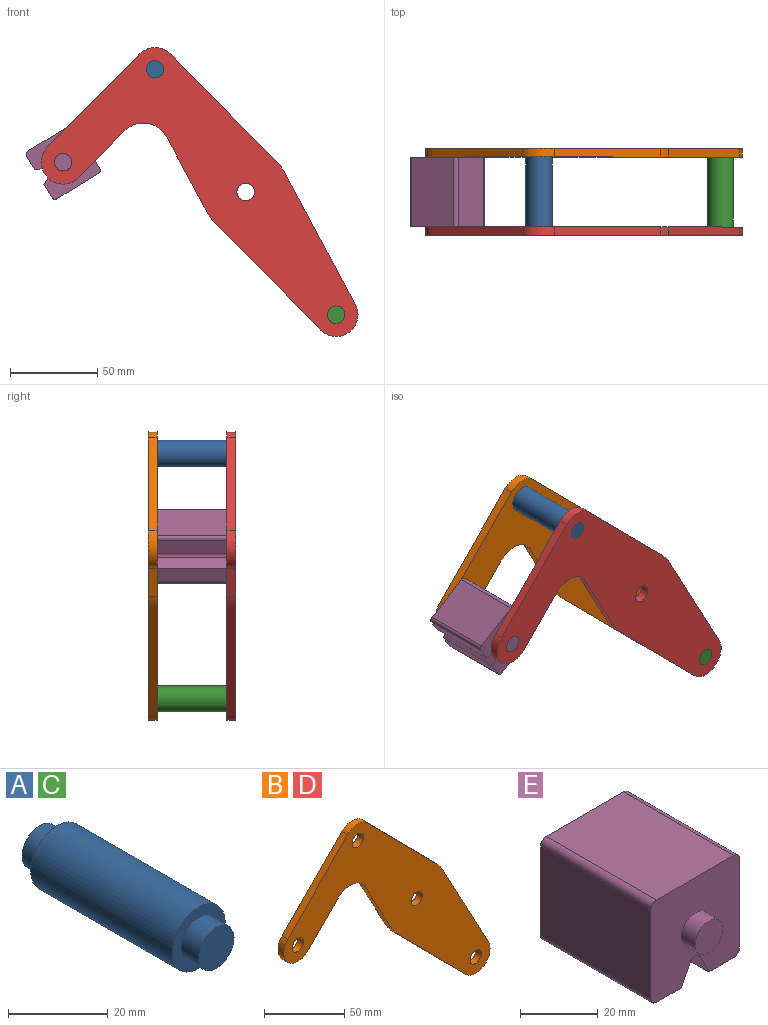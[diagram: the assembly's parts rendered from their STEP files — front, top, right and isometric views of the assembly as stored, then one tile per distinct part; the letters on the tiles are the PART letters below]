
ASSEMBLY  parts=5 mates=3
PART A: 7 faces, bbox 15x50x15 mm
  f0: cylinder r=7.5mm len=40mm, axis (0,-1,0), area 1885mm2, adj f2,f5
  f1: cylinder r=5mm len=10mm, axis (0,1,0), area 157.1mm2, adj f2,f3
  f2: plane 15x15mm, normal (0,-1,0), area 98.2mm2, adj f0,f1
  f3: plane 10x10mm, normal (0,-1,0), area 78.5mm2, adj f1
  f4: cylinder r=5mm len=10mm, axis (0,-1,0), area 157.1mm2, adj f5,f6
  f5: plane 15x15mm, normal (0,1,0), area 98.2mm2, adj f0,f4
  f6: plane 10x10mm, normal (0,1,0), area 78.5mm2, adj f4
PART B: 18 faces, bbox 181.7x5x165.8 mm
  f0: plane 43.49x23.35mm, normal (-0.88,0,-0.47), area 246.8mm2, adj f1,f14,f16,f17
  f1: cylinder r=25mm len=5.75mm, axis (0,1,0), area 35.8mm2, adj f0,f2,f16,f17
  f2: plane 61.6x60.87mm, normal (-0.71,0,-0.7), area 433mm2, adj f1,f3,f16,f17
  f3: cylinder r=12.5mm len=21.39mm, axis (0,1,0), area 178.4mm2, adj f2,f4,f16,f17
  f4: plane 76.3x40.96mm, normal (0.88,0,0.47), area 433mm2, adj f3,f5,f16,f17
  f5: cylinder r=25mm len=5.75mm, axis (0,1,0), area 35.8mm2, adj f4,f6,f16,f17
  f6: plane 61.6x60.87mm, normal (0.71,0,0.7), area 433mm2, adj f5,f7,f16,f17
  f7: cylinder r=12.5mm len=17.78mm, axis (0,1,0), area 98.9mm2, adj f6,f8,f16,f17
  f8: plane 53.35x52.71mm, normal (-0.71,0,0.7), area 375mm2, adj f7,f9,f16,f17
  f9: cylinder r=12.5mm len=21.39mm, axis (0,1,0), area 196.3mm2, adj f8,f10,f16,f17
  f10: plane 26.86x26.54mm, normal (0.71,0,-0.7), area 188.8mm2, adj f9,f14,f16,f17
  f11: cylinder r=5mm len=10mm, axis (0,1,0), area 157.1mm2, adj f16,f17
  f12: cylinder r=5mm len=10mm, axis (0,1,0), area 157.1mm2, adj f16,f17
  f13: cylinder r=5mm len=10mm, axis (0,1,0), area 157.1mm2, adj f16,f17
  f14: cylinder r=15mm len=23.89mm, axis (0,1,0), area 140.2mm2, adj f0,f10,f16,f17
  f15: cylinder r=5mm len=10mm, axis (0,1,0), area 157.1mm2, adj f16,f17
  f16: plane 181.66x165.78mm, normal (0,-1,0), area 8710.1mm2, adj f0,f1,f2,f3,f4,f5,f6,f7
  f17: plane 181.66x165.78mm, normal (0,1,0), area 8710.1mm2, adj f0,f1,f2,f3,f4,f5,f6,f7
PART C: same geometry as A
PART D: same geometry as B
PART E: 18 faces, bbox 32.1x50x32.1 mm
  f0: plane 40x28.08mm, normal (1,0,0), area 1123.1mm2, adj f4,f10,f13,f14
  f1: plane 40x9.04mm, normal (0,0,-1), area 361.6mm2, adj f2,f4,f10,f14
  f2: plane 40x6.42mm, normal (-0.89,0,-0.45), area 287.2mm2, adj f1,f4,f10,f15
  f3: plane 40x6.42mm, normal (0.89,0,-0.45), area 287.2mm2, adj f4,f5,f10,f15
  f4: plane 32.08x32.08mm, normal (0,-1,0), area 900.6mm2, adj f0,f1,f2,f3,f5,f6,f7,f9
  f5: plane 40x9.04mm, normal (0,0,-1), area 361.6mm2, adj f3,f4,f10,f16
  f6: plane 40x28.08mm, normal (0,0,1), area 1123.1mm2, adj f4,f10,f13,f17
  f7: plane 40x28.08mm, normal (-1,0,0), area 1123.1mm2, adj f4,f10,f16,f17
  f8: plane 10x10mm, normal (0,-1,0), area 78.5mm2, adj f9
  f9: cylinder r=5mm len=10mm, axis (0,1,0), area 157.1mm2, adj f4,f8
  f10: plane 32.08x32.08mm, normal (0,1,0), area 900.6mm2, adj f0,f1,f2,f3,f5,f6,f7,f12
  f11: plane 10x10mm, normal (0,1,0), area 78.5mm2, adj f12
  f12: cylinder r=5mm len=10mm, axis (0,-1,0), area 157.1mm2, adj f10,f11
  f13: cylinder r=2mm len=40mm, axis (0,1,0), area 125.7mm2, adj f0,f4,f6,f10
  f14: cylinder r=2mm len=40mm, axis (0,-1,0), area 125.7mm2, adj f0,f1,f4,f10
  f15: cylinder r=2mm len=40mm, axis (0,1,0), area 177.1mm2, adj f2,f3,f4,f10
  f16: cylinder r=2mm len=40mm, axis (0,1,0), area 125.7mm2, adj f4,f5,f7,f10
  f17: cylinder r=2mm len=40mm, axis (0,-1,0), area 125.7mm2, adj f4,f6,f7,f10
PLACE A t=(0,-20,0)mm
PLACE B t=(0,25,0)mm
PLACE C t=(103.95,-20,-140.78)mm
PLACE D t=(0,-20,0)mm fixed
PLACE E rot(axis=(0,1,0),58.5deg) t=(-64.54,-20,-81.13)mm
MATE fastened B.f7 <-> A.f0  axis (0,-1,0) through (-51.98,20,70.39)mm
MATE fastened C.f0 <-> D.f3  axis (0,-1,0) through (51.98,-20,-70.39)mm
MATE revolute D.f9 <-> E.f9  axis (0,1,0) through (-104.69,-20,17.04)mm
